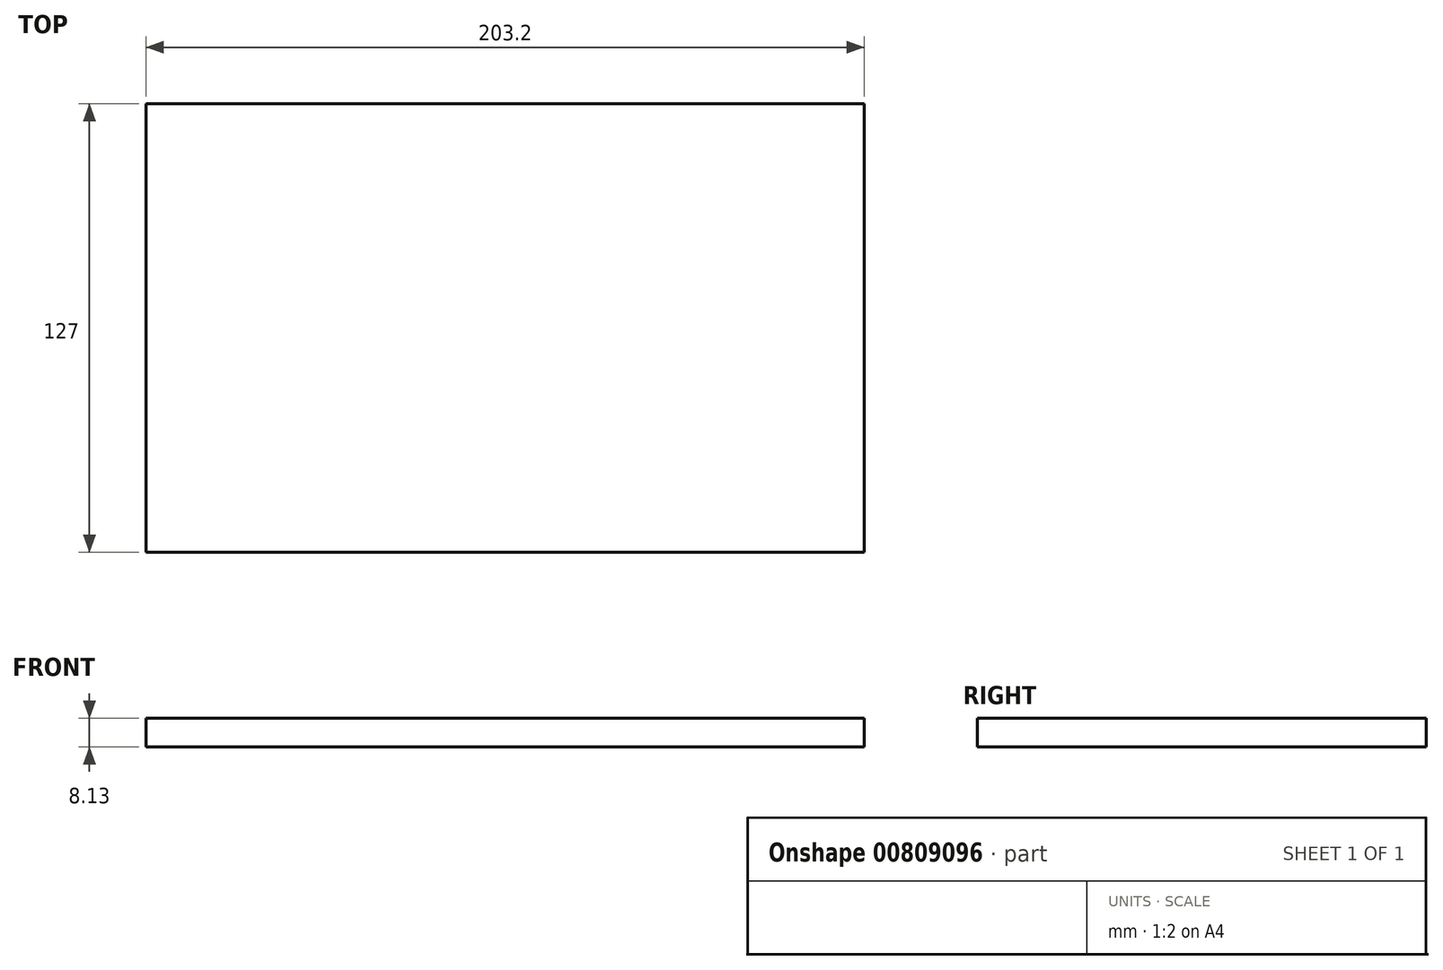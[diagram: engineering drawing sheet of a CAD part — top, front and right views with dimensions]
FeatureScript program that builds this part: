
annotation { "Feature Type Name" : "Feature", "Feature Type Description" : "" }
export const myFeature = defineFeature(function(context is Context, id is Id, definition is map)
    precondition{}
    {
        {
            var Q0;
            Q0=qCreatedBy(makeId("Top.planeOp"),FACE);
            var sketch = newSketch(context, id + "F0", { "sketchPlane" : qUnion([Q0])});
            skLineSegment(sketch, "E0.bottom", {"start": v(0, 0) * mm, "end": v(203.2, 0) * mm});
            skLineSegment(sketch, "E0.top", {"start": v(0, 127) * mm, "end": v(203.2, 127) * mm});
            skLineSegment(sketch, "E0.left", {"start": v(0, 0) * mm, "end": v(0, 127) * mm});
            skLineSegment(sketch, "E0.right", {"start": v(203.2, 0) * mm, "end": v(203.2, 127) * mm});
            skSolve(sketch);
        }
        {
            var Q0;
            Q0=makeQuery(id+"F0.imprint","IMPRINT",FACE,{"disambiguationData":[TD([[makeQuery(id+"F0.imprint","IMPRINT",EDGE,{"derivedFrom":sQuery(id+"F0.wireOp",EDGE,"E0.bottom")}),1.0]])]});
            extrude(context, id + "F1", {"entities" : qUnion([Q0]), "depth" : 8.13 * mm, "offsetDistance" : 25.4 * mm});
        }
    });
